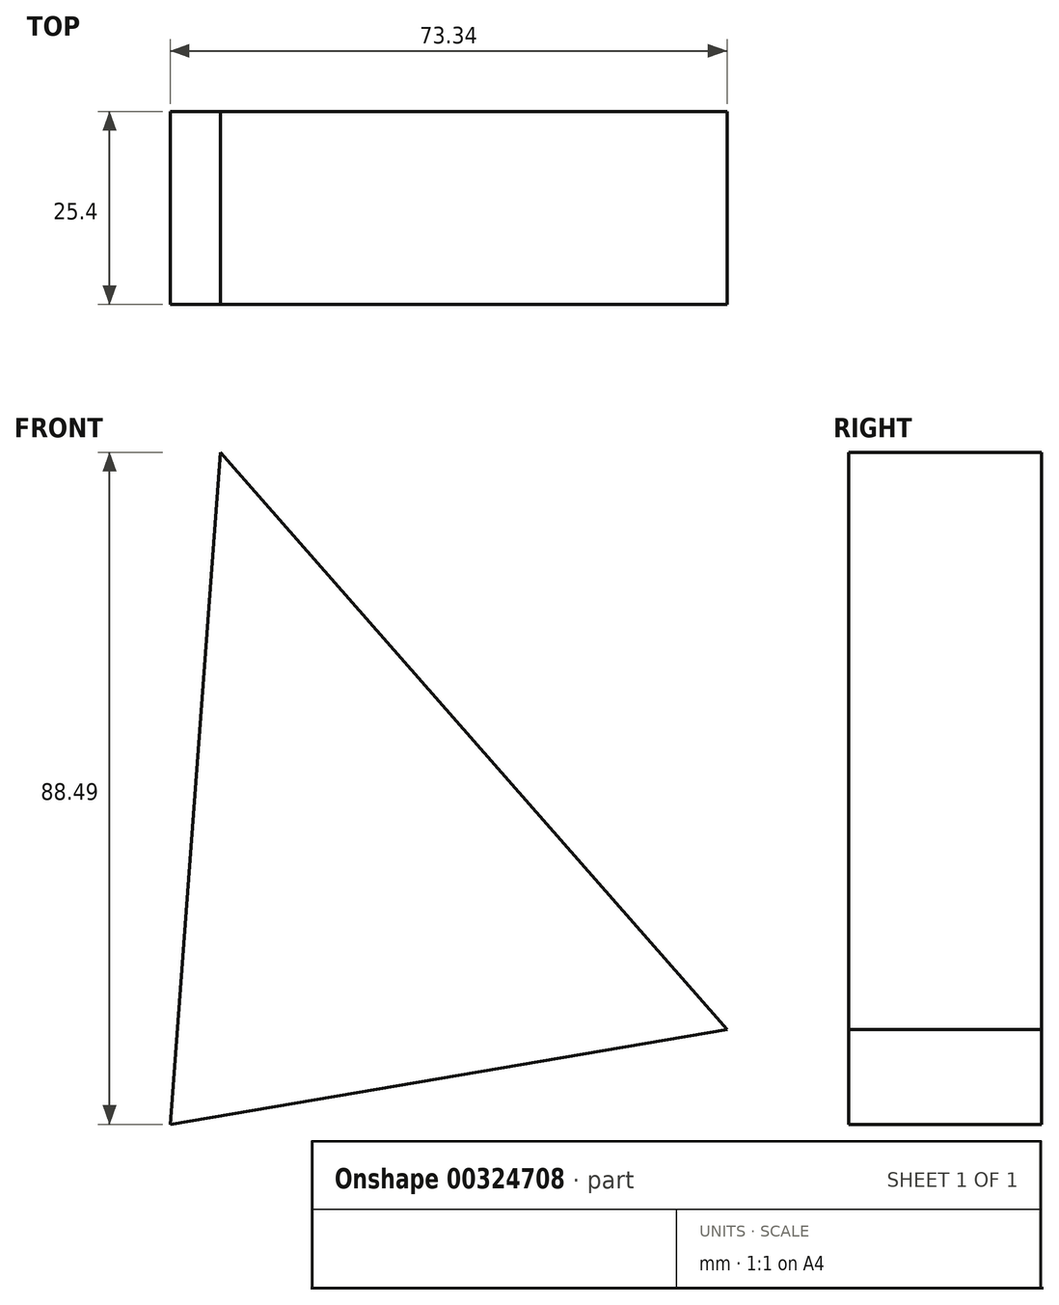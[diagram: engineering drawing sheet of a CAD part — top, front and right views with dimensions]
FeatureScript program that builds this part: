
annotation { "Feature Type Name" : "Feature", "Feature Type Description" : "" }
export const myFeature = defineFeature(function(context is Context, id is Id, definition is map)
    precondition{}
    {
        {
            var Q0;
            Q0=qCreatedBy(makeId("Front.planeOp"),FACE);
            var sketch = newSketch(context, id + "F0", { "sketchPlane" : qUnion([Q0])});
            skLineSegment(sketch, "E0", {"start": v(-66.72, 75.98) * mm, "end": v(0, 0) * mm});
            skLineSegment(sketch, "E1", {"start": v(0, 0) * mm, "end": v(-73.34, -12.51) * mm});
            skLineSegment(sketch, "E2", {"start": v(-73.34, -12.51) * mm, "end": v(-66.72, 75.98) * mm});
            skLineSegment(sketch, "E3", {"start": v(0, 0) * mm, "end": v(0, 30.56) * mm});
            skLineSegment(sketch, "E4", {"start": v(0, 30.56) * mm, "end": v(-73.34, -12.51) * mm});
            skLineSegment(sketch, "E5", {"start": v(0, 30.56) * mm, "end": v(-66.72, 75.98) * mm});
            skSolve(sketch);
        }
        {
            var Q0;
            {var subQ0=sQuery(id+"F0.wireOp",EDGE,"E1");Q0=makeQuery(id+"F0.imprint","IMPRINT",FACE,{"disambiguationData":[TD([[makeQuery(id+"F0.imprint","IMPRINT",EDGE,{"derivedFrom":subQ0}),-1.0]])]});}
            var Q1;
            {var subQ0=sQuery(id+"F0.wireOp",EDGE,"E2");Q1=makeQuery(id+"F0.imprint","IMPRINT",FACE,{"disambiguationData":[TD([[makeQuery(id+"F0.imprint","IMPRINT",EDGE,{"derivedFrom":subQ0}),-1.0]])]});}
            extrude(context, id + "F1", {"entities" : qUnion([Q0, Q1]), "depth" : 25.4 * mm});
        }
    });
